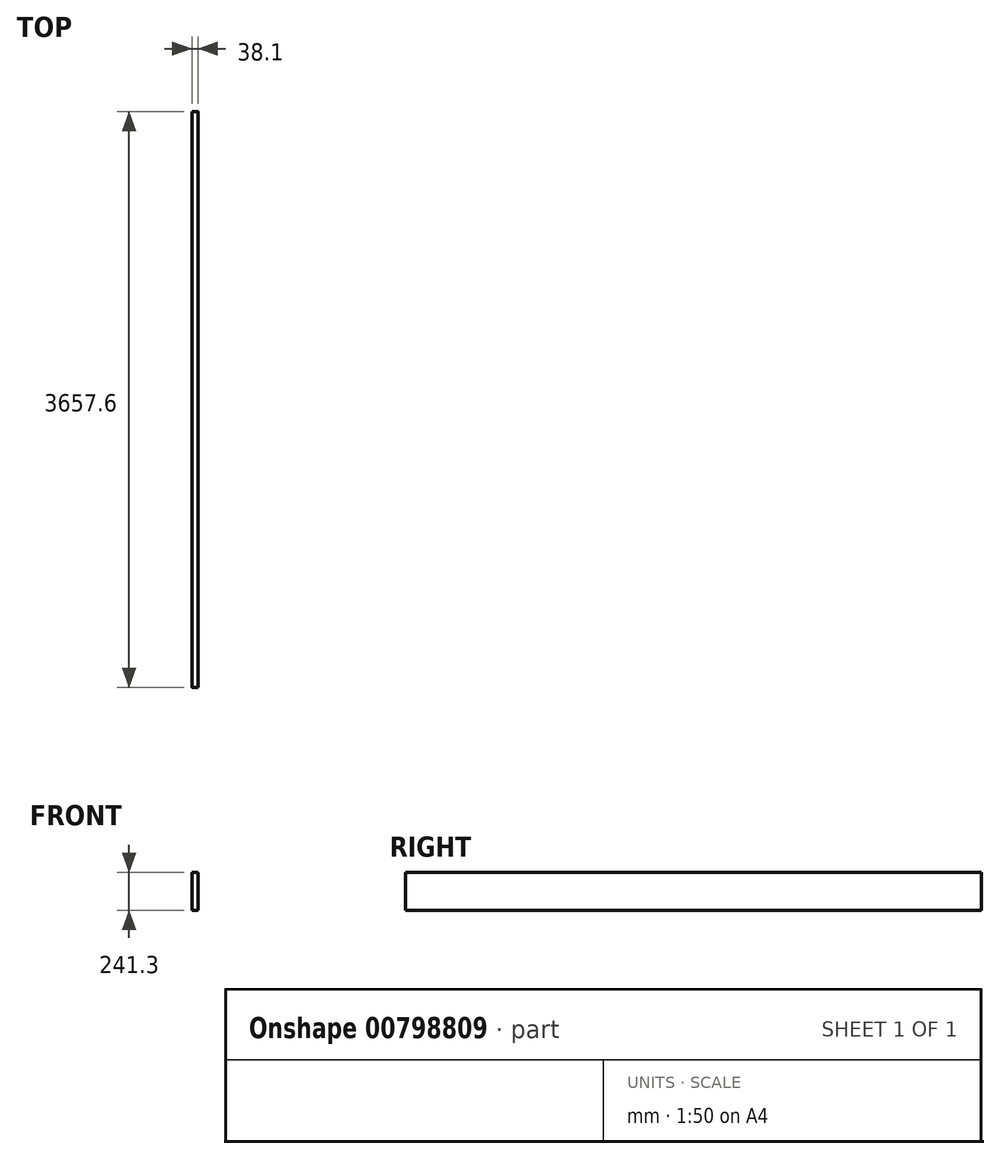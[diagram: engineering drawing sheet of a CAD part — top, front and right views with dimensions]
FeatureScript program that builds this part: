
annotation { "Feature Type Name" : "Feature", "Feature Type Description" : "" }
export const myFeature = defineFeature(function(context is Context, id is Id, definition is map)
    precondition{}
    {
        {
            var Q0;
            Q0=qCreatedBy(makeId("Front.planeOp"),FACE);
            var sketch = newSketch(context, id + "F0", { "sketchPlane" : qUnion([Q0])});
            skLineSegment(sketch, "E0.bottom", {"start": v(-14.22, 120.65) * mm, "end": v(14.22, 120.65) * mm});
            skLineSegment(sketch, "E0.top", {"start": v(-14.22, -120.65) * mm, "end": v(14.22, -120.65) * mm});
            skLineSegment(sketch, "E0.left", {"start": v(-19.05, 115.82) * mm, "end": v(-19.05, -115.82) * mm});
            skLineSegment(sketch, "E0.right", {"start": v(19.05, 115.82) * mm, "end": v(19.05, -115.82) * mm});
            skPoint(sketch, "E0.middle", {"position": v(0, 0) * mm});
            skPoint(sketch, "E1.visualSharp", {"position": v(-19.05, 120.65) * mm});
            skArc(sketch, "E1.filletArc", {"start": v(-14.22, 120.65) * mm, "mid": v(-17.64, 119.24) * mm, "end": v(-19.05, 115.82) * mm});
            skPoint(sketch, "E2.visualSharp", {"position": v(19.05, 120.65) * mm});
            skArc(sketch, "E2.filletArc", {"start": v(19.05, 115.82) * mm, "mid": v(17.64, 119.24) * mm, "end": v(14.22, 120.65) * mm});
            skPoint(sketch, "E3.visualSharp", {"position": v(19.05, -120.65) * mm});
            skArc(sketch, "E3.filletArc", {"start": v(14.22, -120.65) * mm, "mid": v(17.64, -119.24) * mm, "end": v(19.05, -115.82) * mm});
            skPoint(sketch, "E4.visualSharp", {"position": v(-19.05, -120.65) * mm});
            skArc(sketch, "E4.filletArc", {"start": v(-19.05, -115.82) * mm, "mid": v(-17.64, -119.24) * mm, "end": v(-14.22, -120.65) * mm});
            skSolve(sketch);
        }
        {
            var Q0;
            Q0=makeQuery(id+"F0.imprint","IMPRINT",FACE,{"disambiguationData":[TD([[makeQuery(id+"F0.imprint","IMPRINT",EDGE,{"derivedFrom":sQuery(id+"F0.wireOp",EDGE,"E0.bottom")}),-1.0]])]});
            extrude(context, id + "F1", {"entities" : qUnion([Q0]), "endBound" : BoundingType.SYMMETRIC, "depth" : 3657.6 * mm, "offsetDistance" : 25.4 * mm});
        }
    });
